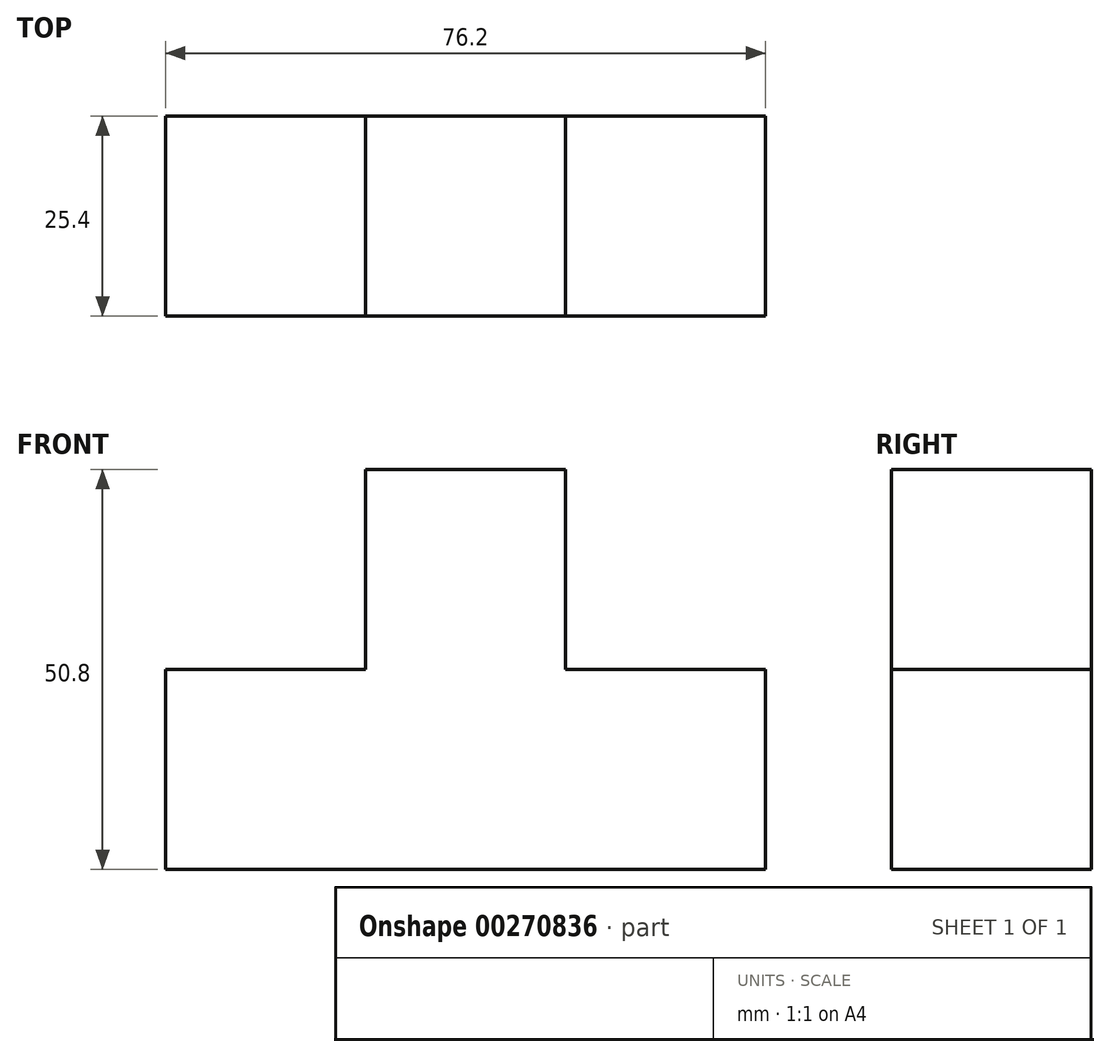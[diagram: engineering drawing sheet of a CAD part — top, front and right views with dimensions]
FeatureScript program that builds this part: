
annotation { "Feature Type Name" : "Feature", "Feature Type Description" : "" }
export const myFeature = defineFeature(function(context is Context, id is Id, definition is map)
    precondition{}
    {
        {
            var Q0;
            Q0=qCreatedBy(makeId("Front.planeOp"),FACE);
            var sketch = newSketch(context, id + "F0", { "sketchPlane" : qUnion([Q0])});
            skLineSegment(sketch, "E0", {"start": v(0, 0) * mm, "end": v(-76.2, 0) * mm});
            skLineSegment(sketch, "E1", {"start": v(-76.2, 0) * mm, "end": v(-76.2, 25.4) * mm});
            skLineSegment(sketch, "E2", {"start": v(-76.2, 25.4) * mm, "end": v(-50.8, 25.4) * mm});
            skLineSegment(sketch, "E3", {"start": v(-50.8, 25.4) * mm, "end": v(-50.8, 50.8) * mm});
            skLineSegment(sketch, "E4", {"start": v(0, 0) * mm, "end": v(0, 25.4) * mm});
            skLineSegment(sketch, "E5", {"start": v(0, 25.4) * mm, "end": v(-25.4, 25.4) * mm});
            skLineSegment(sketch, "E6", {"start": v(-25.4, 25.4) * mm, "end": v(-25.4, 50.8) * mm});
            skLineSegment(sketch, "E7", {"start": v(-50.8, 50.8) * mm, "end": v(-25.4, 50.8) * mm});
            skSolve(sketch);
        }
        {
            var Q0;
            Q0 = qSketchRegion(id + "F0", true);
            extrude(context, id + "F1", {"entities" : qUnion([Q0]), "depth" : 25.4 * mm});
        }
    });
